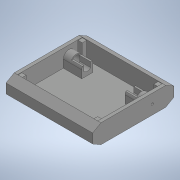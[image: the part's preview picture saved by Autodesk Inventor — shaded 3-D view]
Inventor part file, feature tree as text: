
AUTODESK INVENTOR PART (.ipt)
format: ipt  version: 2020 (Build 240168000, 168)  size: 227,840 bytes
history: native  units: in
note: dims shown in document units (in); Inventor stores cm internally (conversion verified against a paired STEP export)
features: extrude x6, sketch x6, projected_geometry x4, mirror x1
ambient origin geometry x8: Origin, YZ Plane, XZ Plane, XY Plane, X Axis, Y Axis, Z Axis, Center Point
bodies: Solid1 (feature_tree)
feature tree (17):
  extrude  "Extrusion1"  Depth=5.9055in
  extrude  "Extrusion2"  TaperAngle=0.0deg  [1 undecoded]
  extrude  "Extrusion3"  Depth=1.2598in
  extrude  "Extrusion4"  Depth=0.315in
  extrude  "Extrusion5"  TaperAngle=0.0deg  [1 undecoded]
  extrude  "Extrusion6"  Depth=6.063in
  mirror  "Mirror1"
  sketch  "Sketch1"  dims[d0=1.378in d1=5.9055in]
  sketch  "Sketch2"  dims[d2=6.2992in d3=0.0in]
  projected_geometry  "Projected Loop1"
  sketch  "Sketch3"  dims[d4=0.2362in d5=1.2598in]
  projected_geometry  "Projected Loop2"
  projected_geometry  "Projected Loop3"
  sketch  "Sketch4"  dims[d6=0.0in d8=0.315in]
  sketch  "Sketch5"  dims[d10=1.2205in d11=0.0in]
  projected_geometry  "Projected Loop4"
  sketch  "Sketch6"  dims[d12=0.6496in d13=0.689in d14=1.5748in d15=0.0787in d16=0.5512in d17=0.0in d18=0.6102in d19=0.4803in d20=0.7874in d21=0.0in d22=0.1654in d23=6.063in d24=0.0in]
note: 2 required parameter values undecoded (feature->parameter linkage not recoverable at this tier; creation-order binding heuristic only, values carry confidence <= 0.55)
